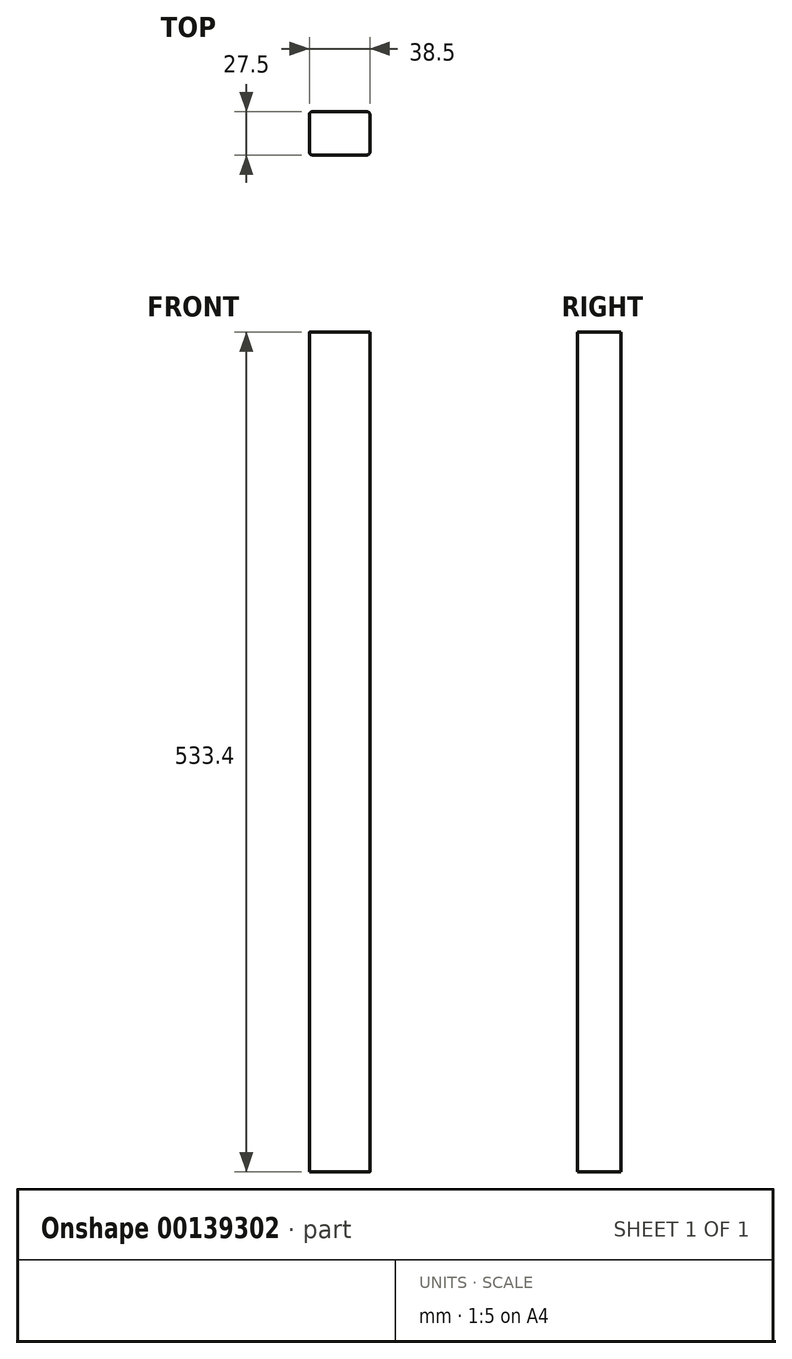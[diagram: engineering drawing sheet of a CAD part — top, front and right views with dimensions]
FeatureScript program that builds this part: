
annotation { "Feature Type Name" : "Feature", "Feature Type Description" : "" }
export const myFeature = defineFeature(function(context is Context, id is Id, definition is map)
    precondition{}
    {
        {
            var Q0;
            Q0=qCreatedBy(makeId("Top.planeOp"),FACE);
            var sketch = newSketch(context, id + "F0", { "sketchPlane" : qUnion([Q0])});
            skLineSegment(sketch, "E0.bottom", {"start": v(6.9, 17.63) * mm, "end": v(45.4, 17.63) * mm});
            skLineSegment(sketch, "E0.top", {"start": v(6.9, -9.87) * mm, "end": v(45.4, -9.87) * mm});
            skLineSegment(sketch, "E0.left", {"start": v(6.9, 17.63) * mm, "end": v(6.9, -9.87) * mm});
            skLineSegment(sketch, "E0.right", {"start": v(45.4, 17.63) * mm, "end": v(45.4, -9.87) * mm});
            skSolve(sketch);
        }
        {
            var Q0;
            Q0=makeQuery(id+"F0.imprint","IMPRINT",FACE,{"disambiguationData":[TD([[makeQuery(id+"F0.imprint","IMPRINT",EDGE,{"derivedFrom":sQuery(id+"F0.wireOp",EDGE,"E0.bottom")}),-1.0]])]});
            extrude(context, id + "F1", {"entities" : qUnion([Q0]), "depth" : 533.4 * mm});
        }
        {
            var Q0;
            Q0=makeQuery(id+"F1.opExtrude","SWEPT_EDGE",EDGE,{"disambiguationData":[OSD([sQuery(id+"F0.wireOp",EDGE,"E0.top"),sQuery(id+"F0.wireOp",EDGE,"E0.right")])]});
            var Q1;
            Q1=makeQuery(id+"F1.opExtrude","SWEPT_EDGE",EDGE,{"disambiguationData":[OSD([sQuery(id+"F0.wireOp",EDGE,"E0.bottom"),sQuery(id+"F0.wireOp",EDGE,"E0.right")])]});
            var Q2;
            Q2=makeQuery(id+"F1.opExtrude","SWEPT_EDGE",EDGE,{"disambiguationData":[OSD([sQuery(id+"F0.wireOp",EDGE,"E0.top"),sQuery(id+"F0.wireOp",EDGE,"E0.left")])]});
            var Q3;
            Q3=makeQuery(id+"F1.opExtrude","SWEPT_EDGE",EDGE,{"disambiguationData":[OSD([sQuery(id+"F0.wireOp",EDGE,"E0.bottom"),sQuery(id+"F0.wireOp",EDGE,"E0.left")])]});
            fillet(context, id + "F2", {"entities" : qUnion([Q0, Q1, Q2, Q3]), "radius" : 2 * mm, "tangentPropagation" : true, "allowEdgeOverflow" : false});
        }
    });
